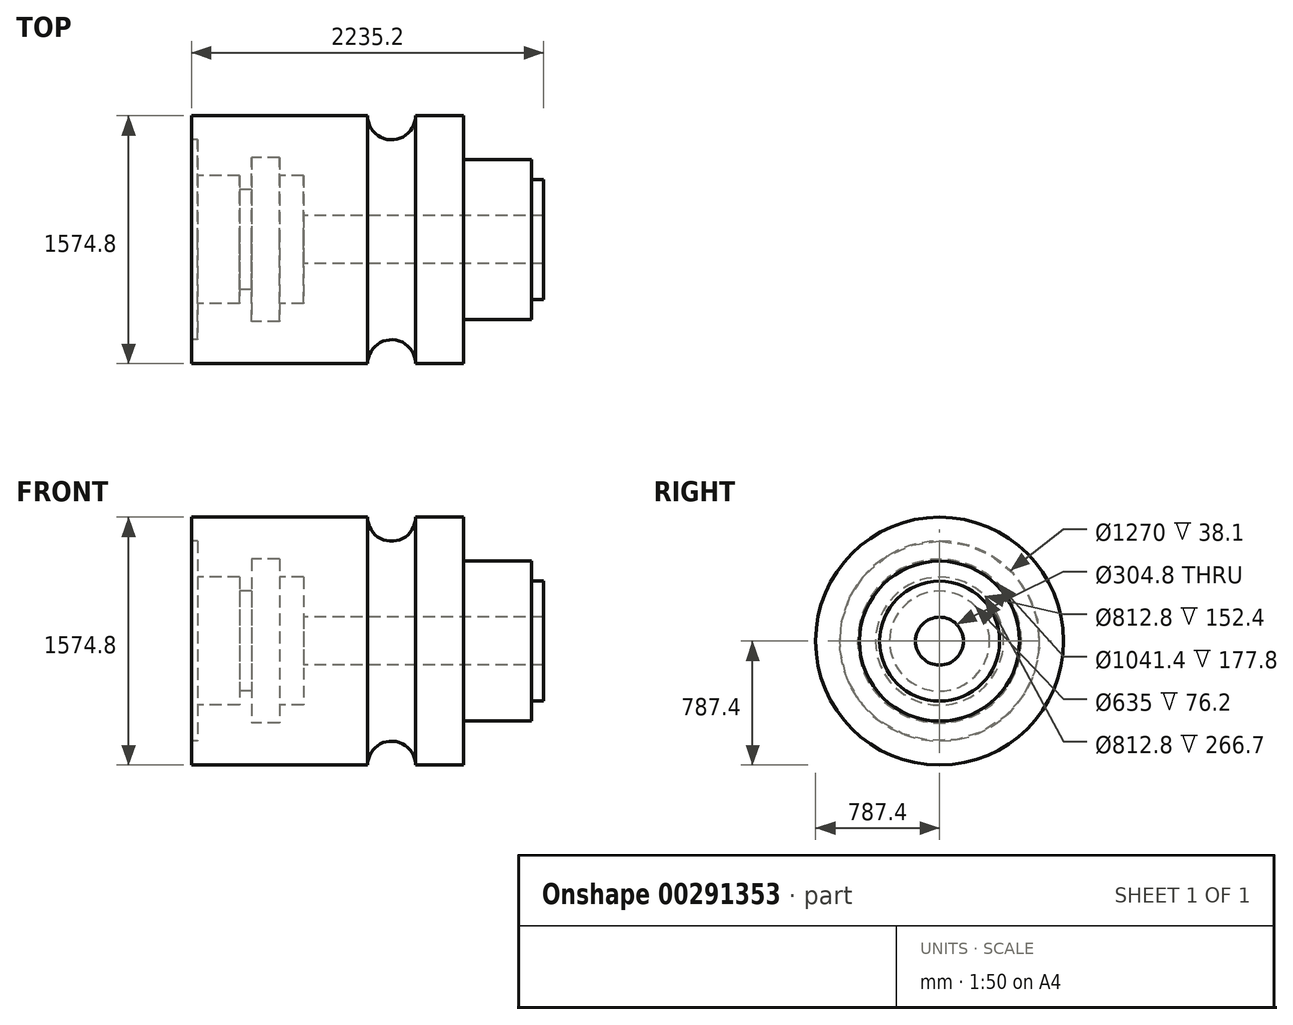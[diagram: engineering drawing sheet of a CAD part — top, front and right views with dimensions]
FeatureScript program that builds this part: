
annotation { "Feature Type Name" : "Feature", "Feature Type Description" : "" }
export const myFeature = defineFeature(function(context is Context, id is Id, definition is map)
    precondition{}
    {
        {
            var Q0;
            Q0=qCreatedBy(makeId("Front.planeOp"),FACE);
            var sketch = newSketch(context, id + "F0", { "sketchPlane" : qUnion([Q0])});
            skLineSegment(sketch, "E0", {"start": v(0, 0) * mm, "end": v(2835.06, 0) * mm, "construction": true});
            skLineSegment(sketch, "E1", {"start": v(0, 0) * mm, "end": v(0, 787.4) * mm});
            skLineSegment(sketch, "E2", {"start": v(0, 787.4) * mm, "end": v(1117.6, 787.4) * mm});
            skLineSegment(sketch, "E3", {"start": v(1727.2, 787.4) * mm, "end": v(1727.2, 508) * mm});
            skLineSegment(sketch, "E4", {"start": v(1727.2, 508) * mm, "end": v(2159, 508) * mm});
            skLineSegment(sketch, "E5", {"start": v(2159, 508) * mm, "end": v(2159, 381) * mm});
            skLineSegment(sketch, "E6", {"start": v(2159, 381) * mm, "end": v(2235.2, 381) * mm});
            skLineSegment(sketch, "E7", {"start": v(2235.2, 381) * mm, "end": v(2235.2, 0) * mm});
            skLineSegment(sketch, "E8", {"start": v(2235.2, 0) * mm, "end": v(0, 0) * mm});
            skArc(sketch, "E9", {"start": v(1117.6, 787.4) * mm, "mid": v(1270, 635) * mm, "end": v(1422.4, 787.4) * mm});
            skLineSegment(sketch, "E10.trimOffspring", {"start": v(1422.4, 787.4) * mm, "end": v(1727.2, 787.4) * mm});
            skSolve(sketch);
        }
        {
            var Q0;
            Q0=makeQuery(id+"F0.imprint","IMPRINT",FACE,{"disambiguationData":[TD([[makeQuery(id+"F0.imprint","IMPRINT",EDGE,{"derivedFrom":sQuery(id+"F0.wireOp",EDGE,"E1")}),-1.0]])]});
            var Q1;
            Q1=sQuery(id+"F0.wireOp",EDGE,"E0");
            revolve(context, id + "F1", {"entities" : qUnion([Q0]), "axis" : qUnion([Q1]), "revolveType" : RevolveType.FULL});
        }
        {
            var Q0;
            Q0=qCreatedBy(makeId("Front.planeOp"),FACE);
            var sketch = newSketch(context, id + "F2", { "sketchPlane" : qUnion([Q0])});
            skLineSegment(sketch, "E11", {"start": v(0, 635) * mm, "end": v(38.1, 635) * mm});
            skLineSegment(sketch, "E12", {"start": v(38.1, 635) * mm, "end": v(38.1, 406.4) * mm});
            skLineSegment(sketch, "E13", {"start": v(38.1, 406.4) * mm, "end": v(304.8, 406.4) * mm});
            skLineSegment(sketch, "E14", {"start": v(304.8, 406.4) * mm, "end": v(304.8, 317.5) * mm});
            skLineSegment(sketch, "E15", {"start": v(304.8, 317.5) * mm, "end": v(381, 317.5) * mm});
            skLineSegment(sketch, "E16", {"start": v(381, 317.5) * mm, "end": v(381, 520.7) * mm});
            skLineSegment(sketch, "E17", {"start": v(381, 520.7) * mm, "end": v(558.8, 520.7) * mm});
            skLineSegment(sketch, "E18", {"start": v(558.8, 520.7) * mm, "end": v(558.8, 406.4) * mm});
            skLineSegment(sketch, "E19", {"start": v(558.8, 406.4) * mm, "end": v(711.2, 406.4) * mm});
            skLineSegment(sketch, "E20", {"start": v(711.2, 406.4) * mm, "end": v(711.2, 152.4) * mm});
            skLineSegment(sketch, "E21", {"start": v(711.2, 152.4) * mm, "end": v(2235.2, 152.4) * mm});
            skLineSegment(sketch, "E22", {"start": v(2235.2, 152.4) * mm, "end": v(2235.2, 0) * mm});
            skLineSegment(sketch, "E23", {"start": v(2235.2, 0) * mm, "end": v(0, 0) * mm});
            skLineSegment(sketch, "E24", {"start": v(0, 0) * mm, "end": v(-447.57, 0) * mm, "construction": true});
            skLineSegment(sketch, "E25", {"start": v(0, 0) * mm, "end": v(0, 635) * mm});
            skSolve(sketch);
        }
        {
            var Q0;
            Q0 = qSketchRegion(id + "F2", true);
            var Q1;
            Q1=sQuery(id+"F2.wireOp",EDGE,"E24");
            revolve(context, id + "F3", {"operationType" : NewBodyOperationType.REMOVE, "entities" : qUnion([Q0]), "axis" : qUnion([Q1]), "revolveType" : RevolveType.FULL, "oppositeDirection" : true});
        }
    });
